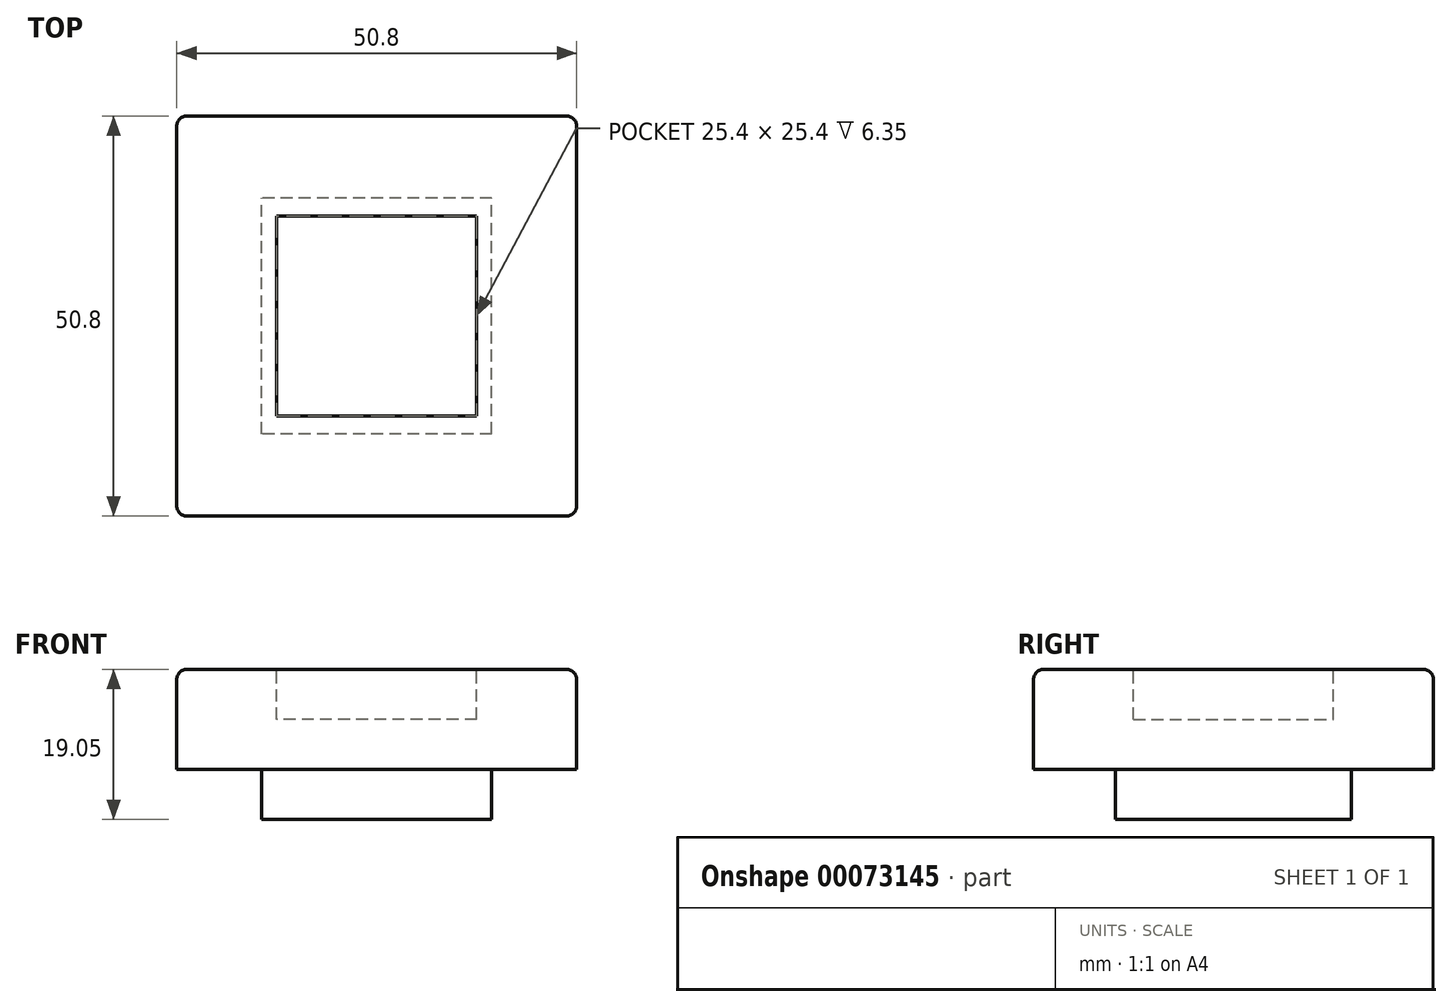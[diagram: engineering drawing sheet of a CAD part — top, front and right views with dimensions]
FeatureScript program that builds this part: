
annotation { "Feature Type Name" : "Feature", "Feature Type Description" : "" }
export const myFeature = defineFeature(function(context is Context, id is Id, definition is map)
    precondition{}
    {
        {
            var Q0;
            Q0=qCreatedBy(makeId("Top.planeOp"),FACE);
            var sketch = newSketch(context, id + "F0", { "sketchPlane" : qUnion([Q0])});
            skLineSegment(sketch, "E0.rect.bottom", {"start": v(14.6, -14.99) * mm, "end": v(-14.6, -14.99) * mm});
            skLineSegment(sketch, "E0.rect.top", {"start": v(14.6, 14.99) * mm, "end": v(-14.6, 14.99) * mm});
            skLineSegment(sketch, "E0.rect.left", {"start": v(14.6, -14.99) * mm, "end": v(14.6, 14.99) * mm});
            skLineSegment(sketch, "E0.rect.right", {"start": v(-14.6, -14.99) * mm, "end": v(-14.6, 14.99) * mm});
            skPoint(sketch, "E0.rect.middle", {"position": v(0, 0) * mm});
            skSolve(sketch);
        }
        {
            var Q0;
            Q0 = qSketchRegion(id + "F0", true);
            extrude(context, id + "F1", {"entities" : qUnion([Q0]), "depth" : 6.35 * mm});
        }
        {
            var Q0;
            Q0=makeQuery(id+"F1.opExtrude","CAP_FACE",FACE,{"disambiguationData":[OSD([sQuery(id+"F0.wireOp",EDGE,"E0.rect.bottom"),sQuery(id+"F0.wireOp",EDGE,"E0.rect.top"),sQuery(id+"F0.wireOp",EDGE,"E0.rect.left"),sQuery(id+"F0.wireOp",EDGE,"E0.rect.right")])],"isStart":false});
            var sketch = newSketch(context, id + "F2", { "sketchPlane" : qUnion([Q0])});
            skLineSegment(sketch, "E1.rect.bottom", {"start": v(25.4, -25.4) * mm, "end": v(-25.4, -25.4) * mm});
            skLineSegment(sketch, "E1.rect.top", {"start": v(25.4, 25.4) * mm, "end": v(-25.4, 25.4) * mm});
            skLineSegment(sketch, "E1.rect.left", {"start": v(25.4, -25.4) * mm, "end": v(25.4, 25.4) * mm});
            skLineSegment(sketch, "E1.rect.right", {"start": v(-25.4, -25.4) * mm, "end": v(-25.4, 25.4) * mm});
            skPoint(sketch, "E1.rect.middle", {"position": v(0, 0) * mm});
            skSolve(sketch);
        }
        {
            var Q0;
            Q0 = qSketchRegion(id + "F2", true);
            extrude(context, id + "F3", {"entities" : qUnion([Q0]), "operationType" : NewBodyOperationType.ADD, "depth" : 12.7 * mm});
        }
        {
            var Q0;
            Q0=makeQuery(id+"F3.opExtrude","CAP_FACE",FACE,{"disambiguationData":[OSD([sQuery(id+"F2.wireOp",EDGE,"E1.rect.bottom"),sQuery(id+"F2.wireOp",EDGE,"E1.rect.top"),sQuery(id+"F2.wireOp",EDGE,"E1.rect.left"),sQuery(id+"F2.wireOp",EDGE,"E1.rect.right")])],"isStart":false});
            var sketch = newSketch(context, id + "F4", { "sketchPlane" : qUnion([Q0])});
            skLineSegment(sketch, "E2.rect.bottom", {"start": v(12.7, -12.7) * mm, "end": v(-12.7, -12.7) * mm});
            skLineSegment(sketch, "E2.rect.top", {"start": v(12.7, 12.7) * mm, "end": v(-12.7, 12.7) * mm});
            skLineSegment(sketch, "E2.rect.left", {"start": v(12.7, -12.7) * mm, "end": v(12.7, 12.7) * mm});
            skLineSegment(sketch, "E2.rect.right", {"start": v(-12.7, -12.7) * mm, "end": v(-12.7, 12.7) * mm});
            skPoint(sketch, "E2.rect.middle", {"position": v(0, 0) * mm});
            skSolve(sketch);
        }
        {
            var Q0;
            Q0 = qSketchRegion(id + "F4", true);
            extrude(context, id + "F5", {"entities" : qUnion([Q0]), "operationType" : NewBodyOperationType.REMOVE, "oppositeDirection" : true, "depth" : 6.35 * mm});
        }
        {
            var Q0;
            Q0=makeQuery(id+"F3.opExtrude","SWEPT_EDGE",EDGE,{"disambiguationData":[OSD([sQuery(id+"F2.wireOp",EDGE,"E1.rect.bottom"),sQuery(id+"F2.wireOp",EDGE,"E1.rect.right")])]});
            var Q1;
            Q1=makeQuery(id+"F3.opExtrude","SWEPT_EDGE",EDGE,{"disambiguationData":[OSD([sQuery(id+"F2.wireOp",EDGE,"E1.rect.bottom"),sQuery(id+"F2.wireOp",EDGE,"E1.rect.left")])]});
            var Q2;
            Q2=makeQuery(id+"F3.opExtrude","SWEPT_EDGE",EDGE,{"disambiguationData":[OSD([sQuery(id+"F2.wireOp",EDGE,"E1.rect.top"),sQuery(id+"F2.wireOp",EDGE,"E1.rect.left")])]});
            var Q3;
            Q3=makeQuery(id+"F3.opExtrude","SWEPT_EDGE",EDGE,{"disambiguationData":[OSD([sQuery(id+"F2.wireOp",EDGE,"E1.rect.top"),sQuery(id+"F2.wireOp",EDGE,"E1.rect.right")])]});
            var Q4;
            Q4=makeQuery(id+"F3.opExtrude","CAP_EDGE",EDGE,{"disambiguationData":[OSD([sQuery(id+"F2.wireOp",EDGE,"E1.rect.bottom")])],"isStart":false});
            var Q5;
            Q5=makeQuery(id+"F3.opExtrude","CAP_EDGE",EDGE,{"disambiguationData":[OSD([sQuery(id+"F2.wireOp",EDGE,"E1.rect.right")])],"isStart":false});
            var Q6;
            Q6=makeQuery(id+"F3.opExtrude","CAP_EDGE",EDGE,{"disambiguationData":[OSD([sQuery(id+"F2.wireOp",EDGE,"E1.rect.top")])],"isStart":false});
            var Q7;
            Q7=makeQuery(id+"F3.opExtrude","CAP_EDGE",EDGE,{"disambiguationData":[OSD([sQuery(id+"F2.wireOp",EDGE,"E1.rect.left")])],"isStart":false});
            fillet(context, id + "F6", {"entities" : qUnion([Q0, Q1, Q2, Q3, Q4, Q5, Q6, Q7]), "radius" : 1.27 * mm, "tangentPropagation" : true, "allowEdgeOverflow" : false});
        }
    });
